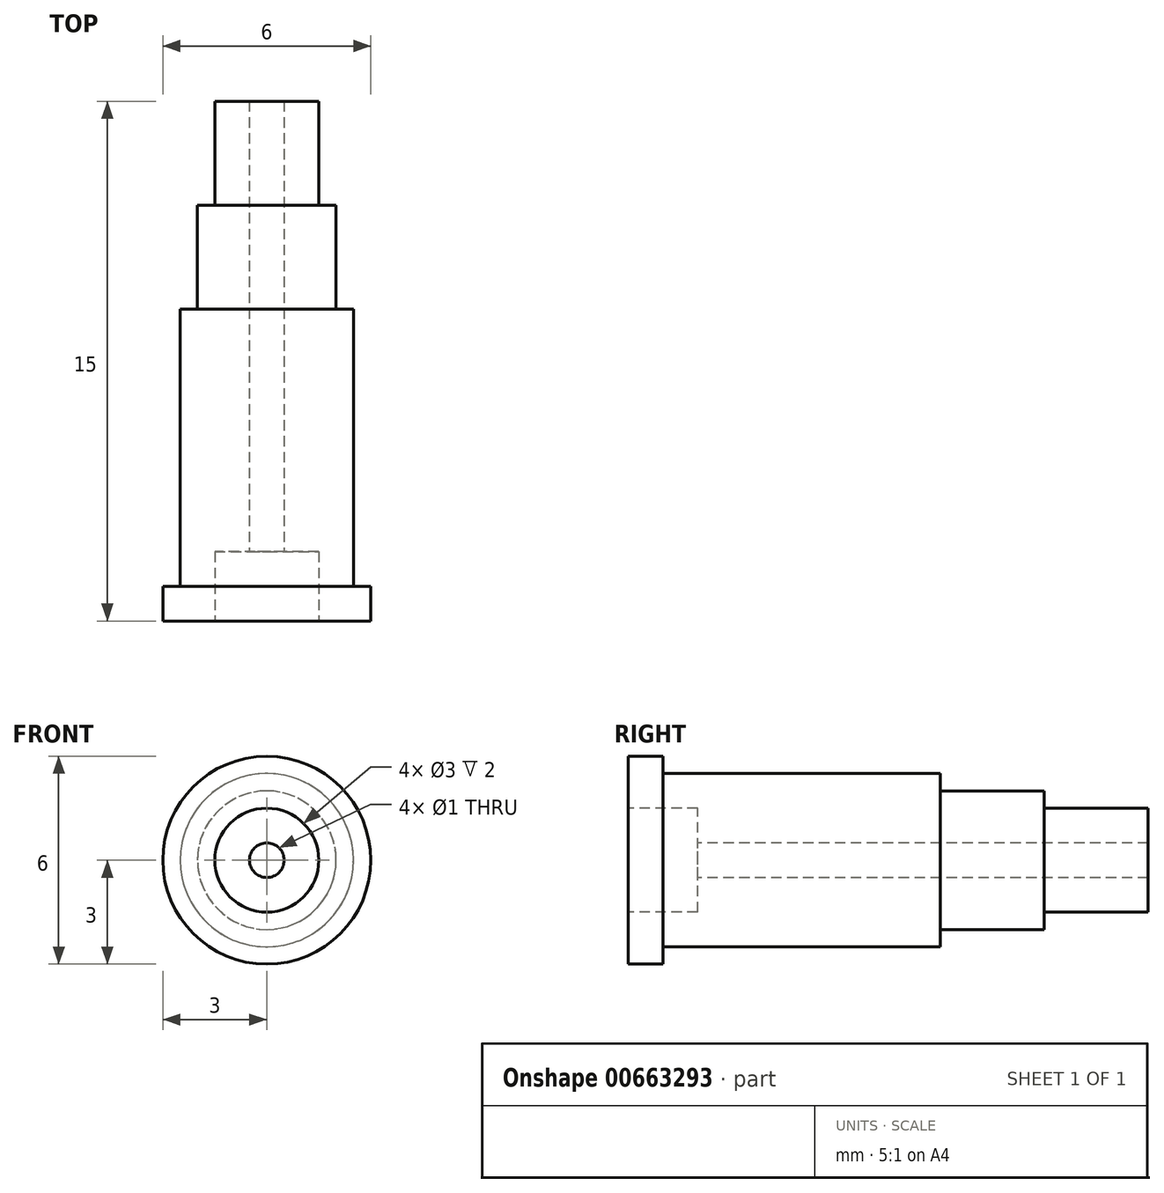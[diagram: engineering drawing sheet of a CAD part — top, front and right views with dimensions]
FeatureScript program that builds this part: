
annotation { "Feature Type Name" : "Feature", "Feature Type Description" : "" }
export const myFeature = defineFeature(function(context is Context, id is Id, definition is map)
    precondition{}
    {
        {
            var Q0;
            Q0=qCreatedBy(makeId("Front.planeOp"),FACE);
            var sketch = newSketch(context, id + "F0", { "sketchPlane" : qUnion([Q0])});
            skCircle(sketch, "E0", {"center": v(0, 0) * mm, "radius": 3 * mm});
            skSolve(sketch);
        }
        {
            var Q0;
            Q0=makeQuery(id+"F0.imprint","IMPRINT",FACE,{"disambiguationData":[TD([[makeQuery(id+"F0.imprint","IMPRINT",EDGE,{"derivedFrom":sQuery(id+"F0.wireOp",EDGE,"E0")}),1.0]])]});
            extrude(context, id + "F1", {"entities" : qUnion([Q0]), "depth" : 15 * mm, "offsetDistance" : 25 * mm});
        }
        {
            var Q0;
            Q0=makeQuery(id+"F1.opExtrude","CAP_FACE",FACE,{"disambiguationData":[OSD([sQuery(id+"F0.wireOp",EDGE,"E0")])],"isStart":false});
            var sketch = newSketch(context, id + "F2", { "sketchPlane" : qUnion([Q0])});
            skCircle(sketch, "E1", {"center": v(0, 0) * mm, "radius": 1.5 * mm});
            skSolve(sketch);
        }
        {
            var Q0;
            Q0=makeQuery(id+"F2.imprint","IMPRINT",FACE,{"disambiguationData":[TD([[makeQuery(id+"F2.imprint","IMPRINT",EDGE,{"derivedFrom":sQuery(id+"F2.wireOp",EDGE,"E1")}),1.0]])]});
            extrude(context, id + "F3", {"entities" : qUnion([Q0]), "operationType" : NewBodyOperationType.REMOVE, "oppositeDirection" : true, "depth" : 2 * mm, "offsetDistance" : 25 * mm});
        }
        {
            var Q0;
            Q0=qCreatedBy(makeId("Right.planeOp"),FACE);
            var sketch = newSketch(context, id + "F4", { "sketchPlane" : qUnion([Q0])});
            skLineSegment(sketch, "E2", {"start": v(-28.14, 0) * mm, "end": v(11.23, 0) * mm, "construction": true});
            skLineSegment(sketch, "E3.bottom", {"start": v(-3, 3.71) * mm, "end": v(2.88, 3.71) * mm});
            skLineSegment(sketch, "E3.top", {"start": v(-3, 1.5) * mm, "end": v(2.88, 1.5) * mm});
            skLineSegment(sketch, "E3.left", {"start": v(-3, 3.71) * mm, "end": v(-3, 1.5) * mm});
            skLineSegment(sketch, "E3.right", {"start": v(2.88, 3.71) * mm, "end": v(2.88, 1.5) * mm});
            skSolve(sketch);
        }
        {
            var Q0;
            Q0 = qSketchRegion(id + "F4", true);
            var Q1;
            Q1=sQuery(id+"F4.wireOp",EDGE,"E2");
            revolve(context, id + "F5", {"operationType" : NewBodyOperationType.REMOVE, "entities" : qUnion([Q0]), "axis" : qUnion([Q1]), "revolveType" : RevolveType.FULL, "oppositeDirection" : true});
        }
        {
            var Q0;
            Q0=makeQuery(id+"F3.boolean.opBoolean","COPY",FACE,{"derivedFrom":makeQuery(id+"F3.opExtrude","CAP_FACE",FACE,{"disambiguationData":[OSD([sQuery(id+"F2.wireOp",EDGE,"E1")])],"isStart":false})});
            var sketch = newSketch(context, id + "F6", { "sketchPlane" : qUnion([Q0])});
            skCircle(sketch, "E4", {"center": v(0, 0) * mm, "radius": 0.5 * mm});
            skSolve(sketch);
        }
        {
            var Q0;
            Q0=makeQuery(id+"F6.imprint","IMPRINT",FACE,{"disambiguationData":[TD([[makeQuery(id+"F6.imprint","IMPRINT",EDGE,{"derivedFrom":sQuery(id+"F6.wireOp",EDGE,"E4")}),1.0]])]});
            extrude(context, id + "F7", {"entities" : qUnion([Q0]), "operationType" : NewBodyOperationType.REMOVE, "endBound" : BoundingType.THROUGH_ALL, "oppositeDirection" : true, "depth" : 25 * mm, "offsetDistance" : 25 * mm});
        }
        {
            var Q0;
            Q0=qCreatedBy(makeId("Right.planeOp"),FACE);
            var sketch = newSketch(context, id + "F8", { "sketchPlane" : qUnion([Q0])});
            skLineSegment(sketch, "E5.bottom", {"start": v(-14, 4.76) * mm, "end": v(2.15, 4.76) * mm});
            skLineSegment(sketch, "E5.top", {"start": v(-14, 2.5) * mm, "end": v(2.15, 2.5) * mm});
            skLineSegment(sketch, "E5.left", {"start": v(-14, 4.76) * mm, "end": v(-14, 2.5) * mm});
            skLineSegment(sketch, "E5.right", {"start": v(2.15, 4.76) * mm, "end": v(2.15, 2.5) * mm});
            skLineSegment(sketch, "E6", {"start": v(-24.56, 0) * mm, "end": v(9.68, 0) * mm, "construction": true});
            skSolve(sketch);
        }
        {
            var Q0;
            Q0=makeQuery(id+"F8.imprint","IMPRINT",FACE,{"disambiguationData":[TD([[makeQuery(id+"F8.imprint","IMPRINT",EDGE,{"derivedFrom":sQuery(id+"F8.wireOp",EDGE,"E5.bottom")}),-1.0]])]});
            var Q1;
            Q1=sQuery(id+"F8.wireOp",EDGE,"E6");
            revolve(context, id + "F9", {"operationType" : NewBodyOperationType.REMOVE, "entities" : qUnion([Q0]), "axis" : qUnion([Q1]), "revolveType" : RevolveType.FULL, "oppositeDirection" : true});
        }
        {
            var Q0;
            Q0=qCreatedBy(makeId("Right.planeOp"),FACE);
            var sketch = newSketch(context, id + "F10", { "sketchPlane" : qUnion([Q0])});
            skLineSegment(sketch, "E7.bottom", {"start": v(-6, 3.94) * mm, "end": v(-1.5, 3.94) * mm});
            skLineSegment(sketch, "E7.top", {"start": v(-6, 2) * mm, "end": v(-1.5, 2) * mm});
            skLineSegment(sketch, "E7.left", {"start": v(-6, 3.94) * mm, "end": v(-6, 2) * mm});
            skLineSegment(sketch, "E7.right", {"start": v(-1.5, 3.94) * mm, "end": v(-1.5, 2) * mm});
            skLineSegment(sketch, "E8", {"start": v(-21.93, 0) * mm, "end": v(8.8, 0) * mm, "construction": true});
            skSolve(sketch);
        }
        {
            var Q0;
            Q0 = qSketchRegion(id + "F10", true);
            var Q1;
            Q1=sQuery(id+"F10.wireOp",EDGE,"E8");
            revolve(context, id + "F11", {"operationType" : NewBodyOperationType.REMOVE, "entities" : qUnion([Q0]), "axis" : qUnion([Q1]), "revolveType" : RevolveType.FULL, "oppositeDirection" : true});
        }
    });
